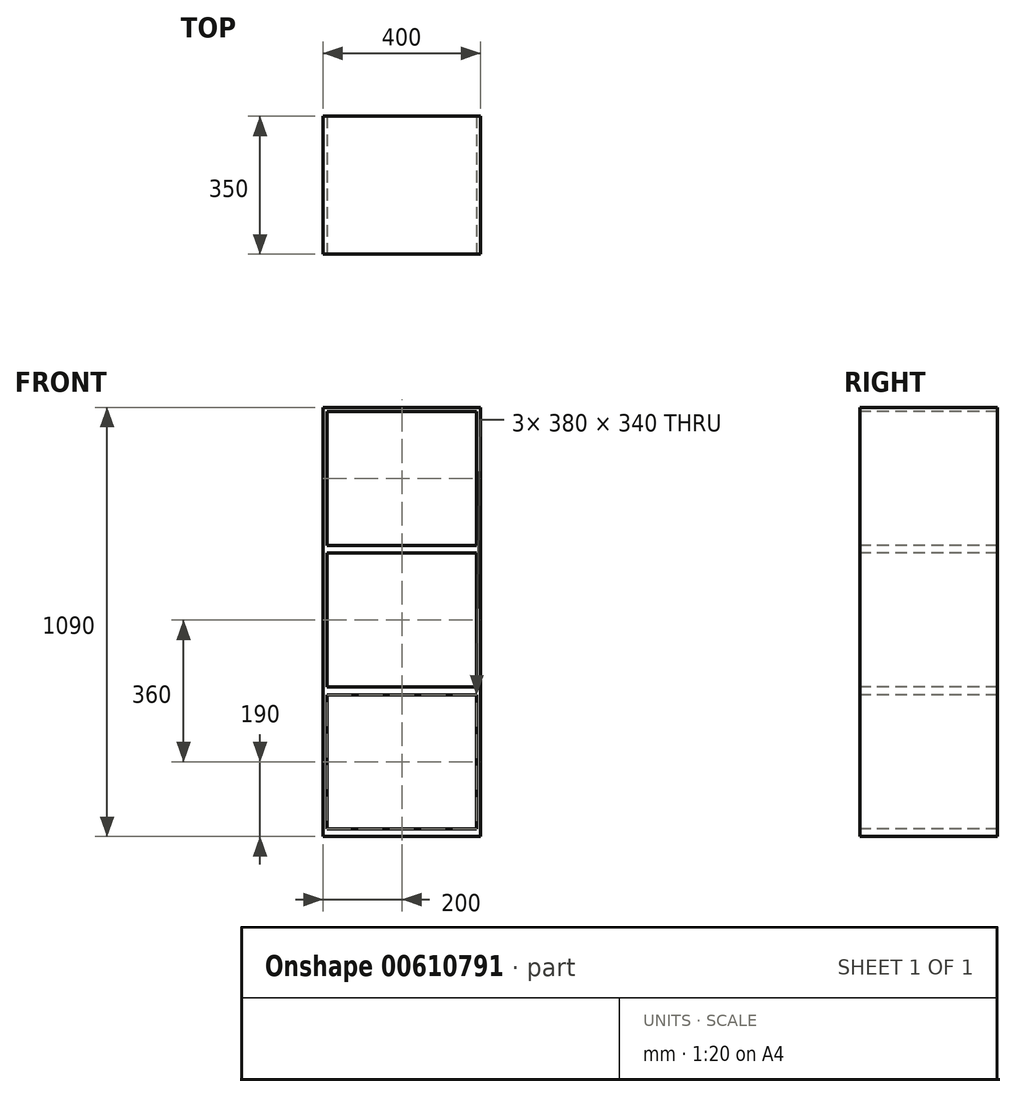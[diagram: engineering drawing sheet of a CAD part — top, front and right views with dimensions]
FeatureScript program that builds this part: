
annotation { "Feature Type Name" : "Feature", "Feature Type Description" : "" }
export const myFeature = defineFeature(function(context is Context, id is Id, definition is map)
    precondition{}
    {
        {
            var Q0;
            Q0=qCreatedBy(makeId("Top.planeOp"),FACE);
            var sketch = newSketch(context, id + "F0", { "sketchPlane" : qUnion([Q0])});
            skLineSegment(sketch, "E0.bottom", {"start": v(0, 0) * mm, "end": v(400, 0) * mm});
            skLineSegment(sketch, "E0.top", {"start": v(0, 350) * mm, "end": v(400, 350) * mm});
            skLineSegment(sketch, "E0.left", {"start": v(0, 0) * mm, "end": v(0, 350) * mm});
            skLineSegment(sketch, "E0.right", {"start": v(400, 0) * mm, "end": v(400, 350) * mm});
            skSolve(sketch);
        }
        {
            var Q0;
            Q0=makeQuery(id+"F0.imprint","IMPRINT",FACE,{"disambiguationData":[TD([[makeQuery(id+"F0.imprint","IMPRINT",EDGE,{"derivedFrom":sQuery(id+"F0.wireOp",EDGE,"E0.bottom")}),1.0]])]});
            extrude(context, id + "F1", {"entities" : qUnion([Q0]), "depth" : 1600 * mm, "offsetDistance" : 25 * mm});
        }
        {
            var Q0;
            Q0=makeQuery(id+"F1.opExtrude","SWEPT_FACE",FACE,{"disambiguationData":[OSD([sQuery(id+"F0.wireOp",EDGE,"E0.bottom")])]});
            var sketch = newSketch(context, id + "F2", { "sketchPlane" : qUnion([Q0])});
            skLineSegment(sketch, "E1", {"start": v(200, 1600) * mm, "end": v(200, 0) * mm});
            skLineSegment(sketch, "E2.bottom", {"start": v(390, 1590) * mm, "end": v(10, 1590) * mm});
            skLineSegment(sketch, "E2.top", {"start": v(390, 1250) * mm, "end": v(10, 1250) * mm});
            skLineSegment(sketch, "E2.left", {"start": v(390, 1590) * mm, "end": v(390, 1250) * mm});
            skLineSegment(sketch, "E2.right", {"start": v(10, 1590) * mm, "end": v(10, 1250) * mm});
            skPoint(sketch, "E2.middle", {"position": v(200, 1420) * mm});
            skLineSegment(sketch, "E3.0.1.0", {"start": v(390, 890) * mm, "end": v(10, 890) * mm});
            skLineSegment(sketch, "E3.0.1.1", {"start": v(10, 1230) * mm, "end": v(10, 890) * mm});
            skLineSegment(sketch, "E3.0.1.2", {"start": v(390, 1230) * mm, "end": v(10, 1230) * mm});
            skLineSegment(sketch, "E3.0.1.3", {"start": v(390, 1230) * mm, "end": v(390, 890) * mm});
            skLineSegment(sketch, "E3.direction1", {"start": v(10, 1250) * mm, "end": v(259.74, 1250) * mm, "construction": true});
            skLineSegment(sketch, "E3.direction2", {"start": v(10, 1250) * mm, "end": v(10, 890) * mm, "construction": true});
            skLineSegment(sketch, "E4.0.0.2", {"start": v(390, 530) * mm, "end": v(10, 530) * mm});
            skLineSegment(sketch, "E4.3.0.2", {"start": v(10, 870) * mm, "end": v(10, 530) * mm});
            skLineSegment(sketch, "E4.6.0.2", {"start": v(390, 870) * mm, "end": v(10, 870) * mm});
            skLineSegment(sketch, "E4.9.0.2", {"start": v(390, 870) * mm, "end": v(390, 530) * mm});
            skSolve(sketch);
        }
        {
            var Q0;
            {var subQ5=sQuery(id+"F2.wireOp",EDGE,"E2.left");Q0=makeQuery(id+"F2.imprint","IMPRINT",FACE,{"disambiguationData":[TD([[makeQuery(id+"F2.imprint","IMPRINT",EDGE,{"derivedFrom":subQ5}),-1.0]])]});}
            var Q1;
            {var subQ5=sQuery(id+"F2.wireOp",EDGE,"E2.right");Q1=makeQuery(id+"F2.imprint","IMPRINT",FACE,{"disambiguationData":[TD([[makeQuery(id+"F2.imprint","IMPRINT",EDGE,{"derivedFrom":subQ5}),1.0]])]});}
            var Q2;
            {var subQ5=sQuery(id+"F2.wireOp",EDGE,"E3.0.1.1");Q2=makeQuery(id+"F2.imprint","IMPRINT",FACE,{"disambiguationData":[TD([[makeQuery(id+"F2.imprint","IMPRINT",EDGE,{"derivedFrom":subQ5}),1.0]])]});}
            var Q3;
            {var subQ5=sQuery(id+"F2.wireOp",EDGE,"E3.0.1.3");Q3=makeQuery(id+"F2.imprint","IMPRINT",FACE,{"disambiguationData":[TD([[makeQuery(id+"F2.imprint","IMPRINT",EDGE,{"derivedFrom":subQ5}),-1.0]])]});}
            var Q4;
            {var subQ5=sQuery(id+"F2.wireOp",EDGE,"E4.9.0.2");Q4=makeQuery(id+"F2.imprint","IMPRINT",FACE,{"disambiguationData":[TD([[makeQuery(id+"F2.imprint","IMPRINT",EDGE,{"derivedFrom":subQ5}),-1.0]])]});}
            var Q5;
            {var subQ5=sQuery(id+"F2.wireOp",EDGE,"E4.3.0.2");Q5=makeQuery(id+"F2.imprint","IMPRINT",FACE,{"disambiguationData":[TD([[makeQuery(id+"F2.imprint","IMPRINT",EDGE,{"derivedFrom":subQ5}),1.0]])]});}
            var Q6;
            {var subQ5=sQuery(id+"F2.wireOp",EDGE,"E4.3.0.3");Q6=makeQuery(id+"F2.imprint","IMPRINT",FACE,{"disambiguationData":[TD([[makeQuery(id+"F2.imprint","IMPRINT",EDGE,{"derivedFrom":subQ5}),1.0]])]});}
            var Q7;
            {var subQ5=sQuery(id+"F2.wireOp",EDGE,"E4.9.0.3");Q7=makeQuery(id+"F2.imprint","IMPRINT",FACE,{"disambiguationData":[TD([[makeQuery(id+"F2.imprint","IMPRINT",EDGE,{"derivedFrom":subQ5}),-1.0]])]});}
            extrude(context, id + "F3", {"entities" : qUnion([Q0, Q1, Q2, Q3, Q4, Q5, Q6, Q7]), "operationType" : NewBodyOperationType.REMOVE, "oppositeDirection" : true, "depth" : 350 * mm, "offsetDistance" : 25 * mm});
        }
        {
            var Q0;
            Q0=makeQuery(id+"F1.opExtrude","CAP_FACE",FACE,{"disambiguationData":[OSD([sQuery(id+"F0.wireOp",EDGE,"E0.bottom"),sQuery(id+"F0.wireOp",EDGE,"E0.top"),sQuery(id+"F0.wireOp",EDGE,"E0.left"),sQuery(id+"F0.wireOp",EDGE,"E0.right")])],"isStart":true});
            extrude(context, id + "F4", {"entities" : qUnion([Q0]), "operationType" : NewBodyOperationType.REMOVE, "oppositeDirection" : true, "depth" : 500 * mm, "offsetDistance" : 25 * mm});
        }
        {
            var Q0;
            Q0=makeQuery(id+"F4.boolean.opBoolean","COPY",FACE,{"derivedFrom":makeQuery(id+"F4.opExtrude","CAP_FACE",FACE,{"disambiguationData":[OSD([sQuery(id+"F0.wireOp",EDGE,"E0.bottom"),sQuery(id+"F0.wireOp",EDGE,"E0.top"),sQuery(id+"F0.wireOp",EDGE,"E0.left"),sQuery(id+"F0.wireOp",EDGE,"E0.right")])],"isStart":false})});
            extrude(context, id + "F5", {"entities" : qUnion([Q0]), "operationType" : NewBodyOperationType.REMOVE, "oppositeDirection" : true, "depth" : 10 * mm, "offsetDistance" : 25 * mm});
        }
    });
